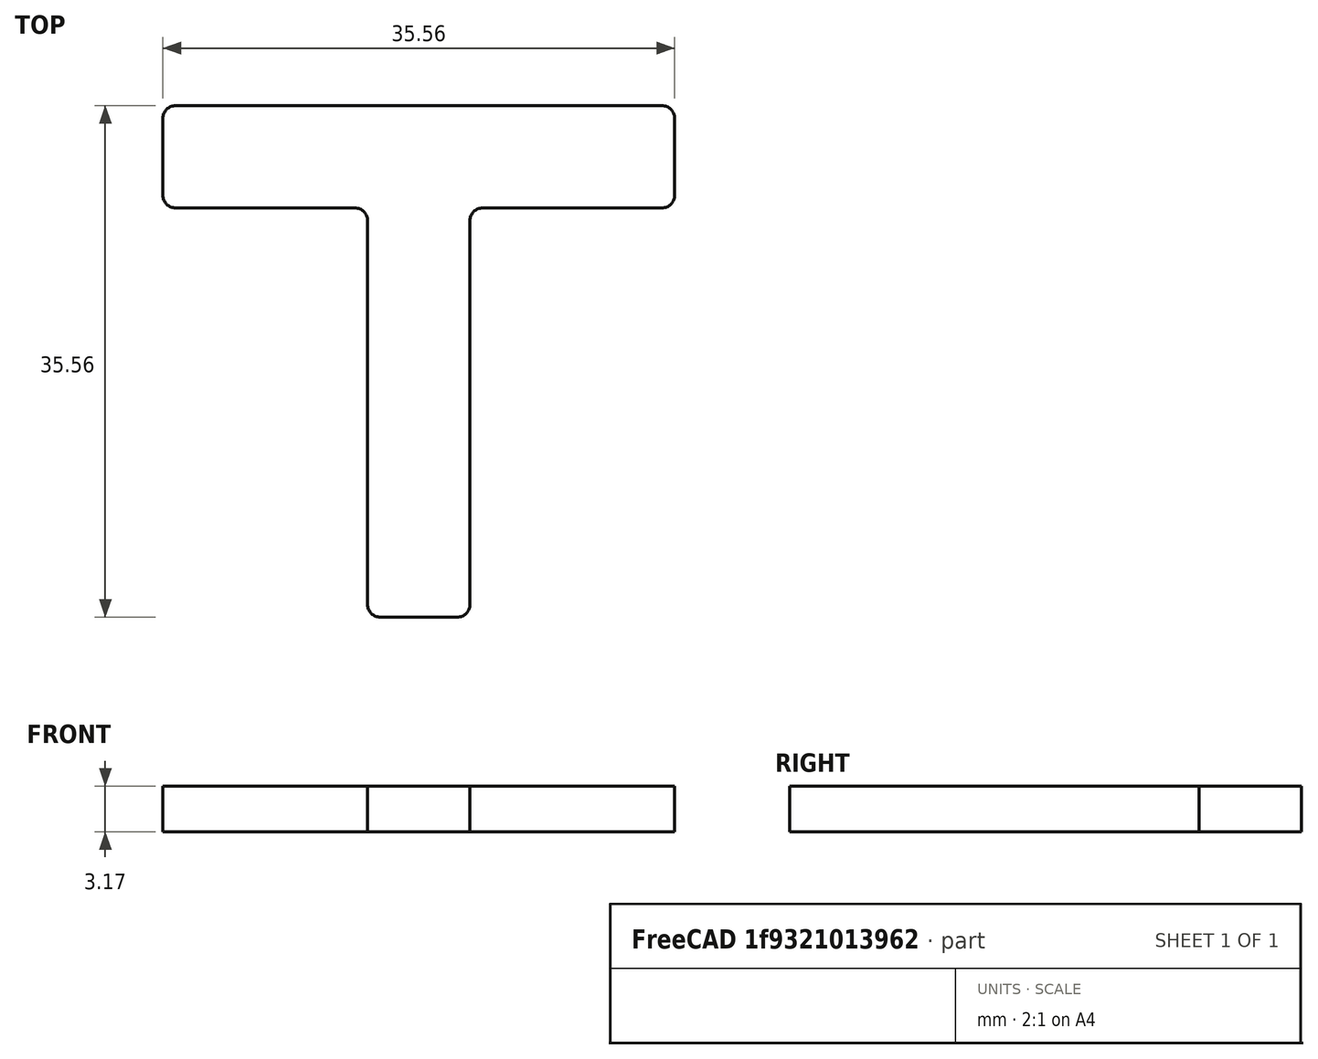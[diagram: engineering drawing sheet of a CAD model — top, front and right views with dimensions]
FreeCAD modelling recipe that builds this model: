
FCSTD DOCUMENT  (FreeCAD 0.20R26720 (Git))
Label: Technician_Template
License: All rights reserved
LicenseURL: http://en.wikipedia.org/wiki/All_rights_reserved
objects: TechDraw::DrawViewDimExtent×2, Sketcher::SketchObject×1, PartDesign::Pad×1, TechDraw::DrawSVGTemplate×1, PartDesign::Fillet×1, PartDesign::Body×1, TechDraw::DrawProjGroupItem×1, TechDraw::DrawProjGroup×1, TechDraw::DrawPage×1
note: 6 computed .brp shape members not serialized (recipe doc carries the construction recipe); baked Part::Feature solids carry a one-line shape summary decoded from their .brp

FEATURE [Sketcher::SketchObject] Sketch
  FullyConstrained = true
  MapMode = 5
  Support = -> [XY_Plane]
  sketch-geometry (8):
    g0: LineSegment StartX=-17.78 StartY=21.336 StartZ=0 EndX=17.78 EndY=21.336 EndZ=0
    g1: LineSegment StartX=17.78 StartY=21.336 StartZ=0 EndX=17.78 EndY=14.224 EndZ=0
    g2: LineSegment StartX=17.78 StartY=14.224 StartZ=0 EndX=3.556 EndY=14.224 EndZ=0
    g3: LineSegment StartX=3.556 StartY=14.224 StartZ=0 EndX=3.556 EndY=-14.224 EndZ=0
    g4: LineSegment StartX=3.556 StartY=-14.224 StartZ=0 EndX=-3.556 EndY=-14.224 EndZ=0
    g5: LineSegment StartX=-3.556 StartY=-14.224 StartZ=0 EndX=-3.556 EndY=14.224 EndZ=0
    g6: LineSegment StartX=-3.556 StartY=14.224 StartZ=0 EndX=-17.78 EndY=14.224 EndZ=0
    g7: LineSegment StartX=-17.78 StartY=14.224 StartZ=0 EndX=-17.78 EndY=21.336 EndZ=0
  constraints (22):
    c: Horizontal(g0)
    c: Coincident(g1,g0)
    c: Vertical(g1)
    c: Coincident(g2,g1)
    c: Horizontal(g2)
    c: Coincident(g3,g2)
    c: Vertical(g3)
    c: Coincident(g4,g3)
    c: Horizontal(g4)
    c: Coincident(g5,g4)
    c: Vertical(g5)
    c: Coincident(g6,g5)
    c: Coincident(g7,g6)
    c: Coincident(g7,g0)
    c: Vertical(g7)
    c: Symmetric(g5,g3,g-1)
    c: Tangent(g2,g6)
    c: Equal(g6,g2)
    c: Equal(g4,g7)
    c: Distance(g1,g7) = 35.56
    c: Distance(g4) = 7.112
    c: Distance(g3,g0) = 35.56
FEATURE [PartDesign::Pad] Pad
  Direction = (0,0,1)
  Length = 3.175
  Length2 = 100.076
  Profile = -> Sketch
  ReferenceAxis = -> Sketch [N_Axis]
  Type = 0
FEATURE [TechDraw::DrawSVGTemplate] Template
  EditableTexts = Designed_by_Name=Design by Matthew; Drawing_number=87f767a2; FC-Date=Dec 2021; FC-SC=1:1; FC-SH=1 of 1; FC-Title=Technician Patch; Subtitle=Tidal Force Robotics; Weight=0.01
  Height = 210
  Orientation = 1
  Width = 297
FEATURE [PartDesign::Fillet] Fillet
  Base = -> Pad [Edge1,Edge20,Edge17,Edge5,Edge14,Edge11,Edge2,Edge8]
  BaseFeature = -> Pad
  Radius = 0.889
  SupportTransform = false
FEATURE [PartDesign::Body] Body  label="Technician Template Body"
  Group = -> [Sketch,Pad,Fillet]
  Origin = -> Origin
  Tip = -> Fillet
FEATURE [TechDraw::DrawProjGroupItem] ProjItem  label="Front"
  CoarseView = false
  Direction = (0,0,1)
  Focus = 100
  HardHidden = false
  IsoCount = 0
  IsoHidden = false
  IsoVisible = false
  LockPosition = true
  Perspective = false
  Rotation = 0
  RotationVector = (1,0,0)
  ScaleType = 2
  SeamHidden = false
  SeamVisible = true
  SmoothHidden = false
  SmoothVisible = true
  Source = -> [Body]
  Type = 0
  X = 0
  XDirection = (1,0,0)
  Y = 0
FEATURE [TechDraw::DrawProjGroup] ProjGroup
  Anchor = -> ProjItem
  AutoDistribute = true
  LockPosition = false
  ProjectionType = 0
  Rotation = 0
  ScaleType = 0
  Source = -> [Body]
  Views = -> [ProjItem]
  X = 148.5
  Y = 105
  spacingX = 14.986
  spacingY = 14.986
FEATURE [TechDraw::DrawViewDimExtent] DimExtent
  Arbitrary = false
  ArbitraryTolerances = false
  CosmeticTags = 4876a07e-5734-4a42-9c70-3ad1e6a7d9bc | d5695a1d-5df9-4573-af45-24d7c8faea45
  DirExtent = 0
  EqualTolerance = true
  FormatSpec = %.3f
  FormatSpecOverTolerance = %+.3f
  FormatSpecUnderTolerance = %+.3f
  Inverted = false
  LockPosition = false
  MeasureType = 1
  OverTolerance = 0
  References2D = -> [ProjItem]
  Rotation = 0
  ScaleType = 0
  Source = -> [ProjItem]
  TheoreticalExact = false
  Type = 1
  UnderTolerance = 0
  X = 0.802663
  Y = -28.3225
FEATURE [TechDraw::DrawViewDimExtent] DimExtent001
  Arbitrary = false
  ArbitraryTolerances = false
  CosmeticTags = cb7f4163-6724-4b0a-a852-f6ca696e9f43 | 79479888-a2d5-4abe-9f57-d4747772a0c1
  DirExtent = 1
  EqualTolerance = true
  FormatSpec = %.3f
  FormatSpecOverTolerance = %+.3f
  FormatSpecUnderTolerance = %+.3f
  Inverted = false
  LockPosition = false
  MeasureType = 1
  OverTolerance = 0
  References2D = -> [ProjItem]
  Rotation = 0
  ScaleType = 0
  Source = -> [ProjItem]
  TheoreticalExact = false
  Type = 2
  UnderTolerance = 0
  X = 31.3039
  Y = 1.83466
FEATURE [TechDraw::DrawPage] Page
  KeepUpdated = true
  NextBalloonIndex = 1
  ProjectionType = 0
  Template = -> Template
  Views = -> [ProjGroup,DimExtent,DimExtent001]
